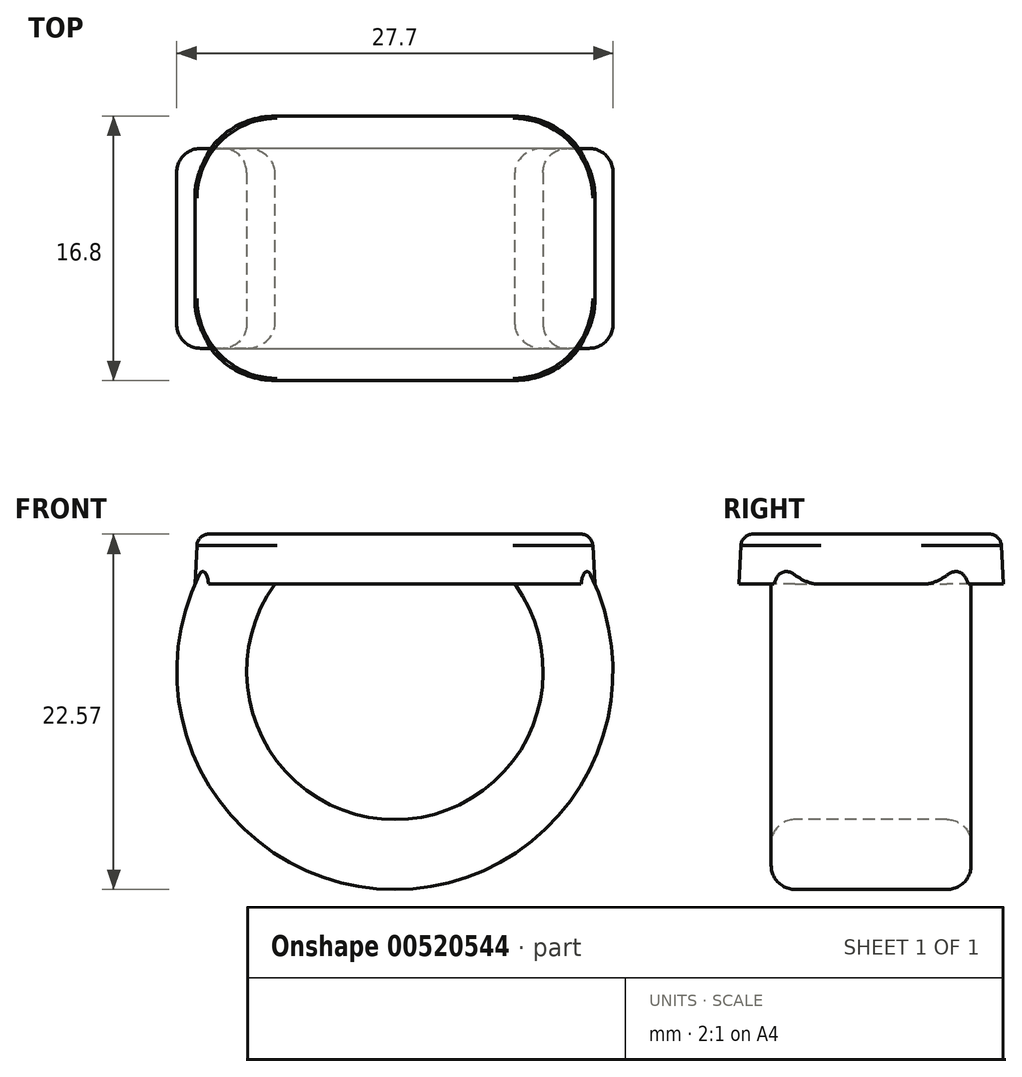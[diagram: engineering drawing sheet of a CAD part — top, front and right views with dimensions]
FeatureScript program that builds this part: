
annotation { "Feature Type Name" : "Feature", "Feature Type Description" : "" }
export const myFeature = defineFeature(function(context is Context, id is Id, definition is map)
    precondition{}
    {
        {
            var Q0;
            Q0=qCreatedBy(makeId("Top.planeOp"),FACE);
            var sketch = newSketch(context, id + "F0", { "sketchPlane" : qUnion([Q0])});
            skLineSegment(sketch, "E0.bottom", {"start": v(-12.7, 8.4) * mm, "end": v(12.7, 8.4) * mm});
            skLineSegment(sketch, "E0.top", {"start": v(-12.7, -8.4) * mm, "end": v(12.7, -8.4) * mm});
            skLineSegment(sketch, "E0.left", {"start": v(-12.7, 8.4) * mm, "end": v(-12.7, -8.4) * mm});
            skLineSegment(sketch, "E0.right", {"start": v(12.7, 8.4) * mm, "end": v(12.7, -8.4) * mm});
            skPoint(sketch, "E0.middle", {"position": v(0, 0) * mm});
            skSolve(sketch);
        }
        {
            var Q0;
            Q0 = qSketchRegion(id + "F0", true);
            extrude(context, id + "F1", {"entities" : qUnion([Q0]), "depth" : 3.17 * mm, "offsetDistance" : 25.4 * mm, "hasDraft" : true, "draftAngle" : 3 * degree, "draftPullDirection" : true});
        }
        {
            var Q0;
            Q0=qCreatedBy(makeId("Front.planeOp"),FACE);
            var sketch = newSketch(context, id + "F2", { "sketchPlane" : qUnion([Q0])});
            skArc(sketch, "E1", {"start": v(-11.43, 0) * mm, "mid": v(0, -18.24) * mm, "end": v(11.43, 0) * mm});
            skSolve(sketch);
        }
        {
            var Q0;
            Q0=makeQuery(id+"F1.opExtrude","CAP_FACE",FACE,{"disambiguationData":[OSD([sQuery(id+"F0.wireOp",EDGE,"E0.bottom"),sQuery(id+"F0.wireOp",EDGE,"E0.top"),sQuery(id+"F0.wireOp",EDGE,"E0.left"),sQuery(id+"F0.wireOp",EDGE,"E0.right")])],"isStart":true});
            var sketch = newSketch(context, id + "F3", { "sketchPlane" : qUnion([Q0])});
            skLineSegment(sketch, "E2.bottom", {"start": v(-12.7, 6.35) * mm, "end": v(-7.62, 6.35) * mm});
            skLineSegment(sketch, "E2.top", {"start": v(-12.7, -6.35) * mm, "end": v(-7.62, -6.35) * mm});
            skLineSegment(sketch, "E2.left", {"start": v(-12.7, 6.35) * mm, "end": v(-12.7, -6.35) * mm});
            skLineSegment(sketch, "E2.right", {"start": v(-7.62, 6.35) * mm, "end": v(-7.62, -6.35) * mm});
            skPoint(sketch, "E2.middle", {"position": v(-10.16, 0) * mm});
            skSolve(sketch);
        }
        {
            var Q0;
            Q0 = qSketchRegion(id + "F3", true);
            var Q1;
            Q1 = qConstructionFilter(qBodyType(qCreatedBy(id + "F2" ,EDGE), BodyType.WIRE), ConstructionObject.NO);
            sweep(context, id + "F4", {"operationType" : NewBodyOperationType.ADD, "profiles" : qUnion([Q0]), "path" : qUnion([Q1])});
        }
        {
            var Q0;
            Q0=qCreatedBy(makeId("Front.planeOp"),FACE);
            var sketch = newSketch(context, id + "F5", { "sketchPlane" : qUnion([Q0])});
            skLineSegment(sketch, "E3.1", {"start": v(9.07, -2.99) * mm, "end": v(11.43, 0) * mm});
            skArc(sketch, "E3.2", {"start": v(9.07, -2.99) * mm, "mid": v(8.48, -1.43) * mm, "end": v(7.62, 0) * mm});
            skLineSegment(sketch, "E4.trimOffspring", {"start": v(7.62, 0) * mm, "end": v(11.43, 0) * mm});
            skPoint(sketch, "E3.0.start.orphan", {"position": v(-12.7, 0) * mm});
            skPoint(sketch, "E5.orphan", {"position": v(-7.62, 0) * mm});
            skPoint(sketch, "E6.orphan", {"position": v(12.7, 0) * mm});
            skSolve(sketch);
        }
        {
            var Q0;
            Q0 = qSketchRegion(id + "F5", true);
            var Q1;
            Q1=makeQuery(id+"F4.opSweep","SWEPT_FACE",FACE,{"disambiguationData":[OSD([sQuery(id+"F2.wireOp",EDGE,"E1"),sQuery(id+"F3.wireOp",EDGE,"E2.bottom")])]});
            var Q2;
            Q2=makeQuery(id+"F4.opSweep","SWEPT_FACE",FACE,{"disambiguationData":[OSD([sQuery(id+"F2.wireOp",EDGE,"E1"),sQuery(id+"F3.wireOp",EDGE,"E2.top")])]});
            extrude(context, id + "F6", {"entities" : qUnion([Q0]), "operationType" : NewBodyOperationType.ADD, "endBound" : BoundingType.UP_TO_SURFACE, "depth" : 25.4 * mm, "endBoundEntityFace" : qUnion([Q1]), "offsetDistance" : 25.4 * mm, "hasSecondDirection" : true, "secondDirectionBound" : SecondDirectionBoundingType.UP_TO_SURFACE, "secondDirectionOppositeDirection" : true, "secondDirectionDepth" : 25.4 * mm, "secondDirectionBoundEntityFace" : qUnion([Q2])});
        }
        {
            var Q0;
            Q0=makeQuery(id+"F1.opExtrude","SWEPT_EDGE",EDGE,{"disambiguationData":[OSD([sQuery(id+"F0.wireOp",EDGE,"E0.top"),sQuery(id+"F0.wireOp",EDGE,"E0.left")])]});
            var Q1;
            Q1=makeQuery(id+"F1.opExtrude","SWEPT_EDGE",EDGE,{"disambiguationData":[OSD([sQuery(id+"F0.wireOp",EDGE,"E0.top"),sQuery(id+"F0.wireOp",EDGE,"E0.right")])]});
            var Q2;
            Q2=makeQuery(id+"F1.opExtrude","SWEPT_EDGE",EDGE,{"disambiguationData":[OSD([sQuery(id+"F0.wireOp",EDGE,"E0.bottom"),sQuery(id+"F0.wireOp",EDGE,"E0.right")])]});
            var Q3;
            Q3=makeQuery(id+"F1.opExtrude","SWEPT_EDGE",EDGE,{"disambiguationData":[OSD([sQuery(id+"F0.wireOp",EDGE,"E0.bottom"),sQuery(id+"F0.wireOp",EDGE,"E0.left")])]});
            fillet(context, id + "F7", {"entities" : qUnion([Q0, Q1, Q2, Q3]), "radius" : 5.08 * mm, "tangentPropagation" : true, "allowEdgeOverflow" : false});
        }
        {
            var Q0;
            Q0=makeQuery(id+"F4.opSweep","SWEPT_EDGE",EDGE,{"disambiguationData":[OSD([sQuery(id+"F0.wireOp",EDGE,"E0.left"),sQuery(id+"F2.wireOp",EDGE,"E1"),sQuery(id+"F3.wireOp",EDGE,"E2.top"),sQuery(id+"F3.wireOp",EDGE,"E2.left")])]});
            var Q1;
            {var subQ0=sQuery(id+"F3.wireOp",EDGE,"E2.top");var subQ1=sQuery(id+"F2.wireOp",EDGE,"E1");Q1=makeQuery(id+"F6.boolean.opBoolean","MERGE",EDGE,{"derivedFrom":[makeQuery(id+"F4.opSweep","SWEPT_EDGE",EDGE,{"disambiguationData":[OSD([subQ1,subQ0,sQuery(id+"F3.wireOp",EDGE,"E2.right")])]}),makeQuery(id+"F6.opExtrude","TWEAK_EDGE",EDGE,{"derivedFrom":[makeQuery(id+"F4.opSweep","SWEPT_FACE",FACE,{"disambiguationData":[OSD([subQ1,subQ0])]}),makeQuery(id+"F5.imprint","IMPRINT",EDGE,{"derivedFrom":sQuery(id+"F5.wireOp",EDGE,"E3.2")})]})]});}
            var Q2;
            {var subQ0=sQuery(id+"F3.wireOp",EDGE,"E2.bottom");var subQ1=sQuery(id+"F2.wireOp",EDGE,"E1");Q2=makeQuery(id+"F6.boolean.opBoolean","MERGE",EDGE,{"derivedFrom":[makeQuery(id+"F4.opSweep","SWEPT_EDGE",EDGE,{"disambiguationData":[OSD([subQ1,subQ0,sQuery(id+"F3.wireOp",EDGE,"E2.right")])]}),makeQuery(id+"F6.opExtrude","TWEAK_EDGE",EDGE,{"derivedFrom":[makeQuery(id+"F4.opSweep","SWEPT_FACE",FACE,{"disambiguationData":[OSD([subQ1,subQ0])]}),makeQuery(id+"F5.imprint","IMPRINT",EDGE,{"derivedFrom":sQuery(id+"F5.wireOp",EDGE,"E3.2")})]})]});}
            var Q3;
            Q3=makeQuery(id+"F4.opSweep","SWEPT_EDGE",EDGE,{"disambiguationData":[OSD([sQuery(id+"F0.wireOp",EDGE,"E0.left"),sQuery(id+"F2.wireOp",EDGE,"E1"),sQuery(id+"F3.wireOp",EDGE,"E2.bottom"),sQuery(id+"F3.wireOp",EDGE,"E2.left")])]});
            fillet(context, id + "F8", {"entities" : qUnion([Q0, Q1, Q2, Q3]), "radius" : 1.52 * mm, "tangentPropagation" : true, "allowEdgeOverflow" : false});
        }
        {
            var Q0;
            Q0=makeQuery(id+"F1.opExtrude","CAP_FACE",FACE,{"disambiguationData":[OSD([sQuery(id+"F0.wireOp",EDGE,"E0.bottom"),sQuery(id+"F0.wireOp",EDGE,"E0.top"),sQuery(id+"F0.wireOp",EDGE,"E0.left"),sQuery(id+"F0.wireOp",EDGE,"E0.right")])],"isStart":false});
            fillet(context, id + "F9", {"entities" : qUnion([Q0]), "radius" : 0.76 * mm, "tangentPropagation" : true, "allowEdgeOverflow" : false});
        }
    });
